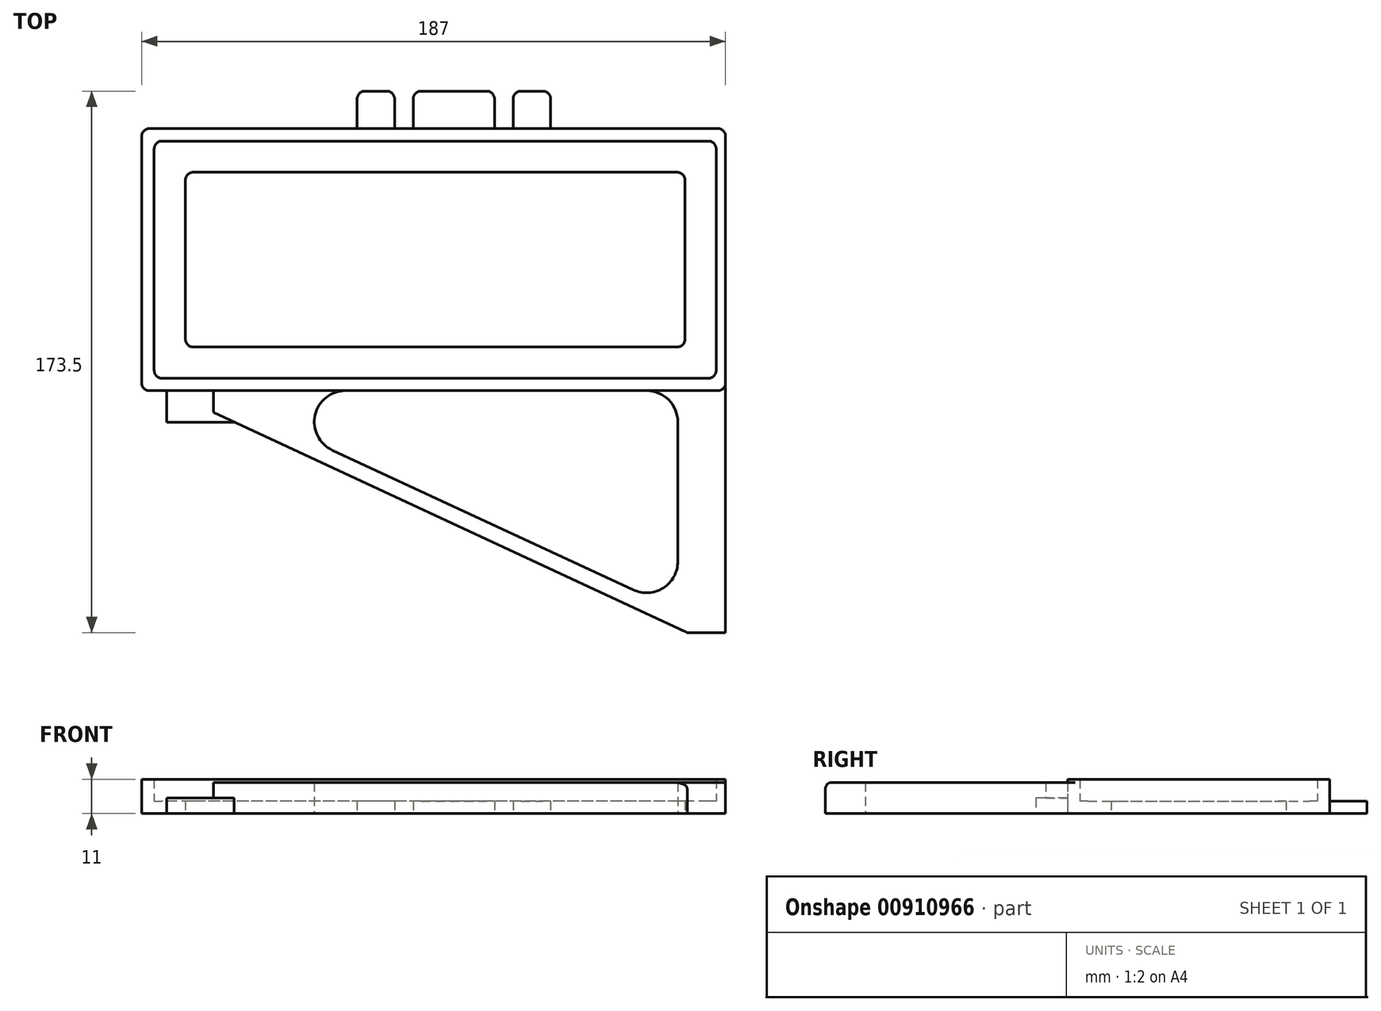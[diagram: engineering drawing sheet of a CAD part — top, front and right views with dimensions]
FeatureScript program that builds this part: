
annotation { "Feature Type Name" : "Feature", "Feature Type Description" : "" }
export const myFeature = defineFeature(function(context is Context, id is Id, definition is map)
    precondition{}
    {
        {
            var Q0;
            Q0=qCreatedBy(makeId("Top.planeOp"),FACE);
            var sketch = newSketch(context, id + "F0", { "sketchPlane" : qUnion([Q0])});
            skLineSegment(sketch, "E0.bottom", {"start": v(87.5, 0) * mm, "end": v(-87.5, 0) * mm});
            skLineSegment(sketch, "E0.top", {"start": v(87.5, 76) * mm, "end": v(-87.5, 76) * mm});
            skLineSegment(sketch, "E0.left", {"start": v(90, 2.5) * mm, "end": v(90, 73.5) * mm});
            skLineSegment(sketch, "E0.right", {"start": v(-90, 2.5) * mm, "end": v(-90, 73.5) * mm});
            skLineSegment(sketch, "E1.0", {"start": v(102, 80) * mm, "end": v(-74, 80) * mm});
            skLineSegment(sketch, "E2.0", {"start": v(-94, 0) * mm, "end": v(-94, 76) * mm});
            skLineSegment(sketch, "E3.0", {"start": v(67.7, -4) * mm, "end": v(-28.7, -4) * mm});
            skLineSegment(sketch, "E4.0", {"start": v(93, 0) * mm, "end": v(93, 76) * mm});
            skLineSegment(sketch, "E5", {"start": v(-74, 80) * mm, "end": v(-91.5, 80) * mm});
            skLineSegment(sketch, "E6", {"start": v(-94, 76) * mm, "end": v(-94, 77.5) * mm});
            skLineSegment(sketch, "E7", {"start": v(-94, -1.5) * mm, "end": v(-94, 0) * mm});
            skLineSegment(sketch, "E8", {"start": v(-88, -4) * mm, "end": v(-91.5, -4) * mm});
            skLineSegment(sketch, "E9", {"start": v(90.5, 80) * mm, "end": v(102, 80) * mm});
            skLineSegment(sketch, "E10", {"start": v(93, 77.5) * mm, "end": v(93, 76) * mm});
            skLineSegment(sketch, "E11", {"start": v(88, -4) * mm, "end": v(90.5, -4) * mm});
            skLineSegment(sketch, "E12", {"start": v(93, -1.5) * mm, "end": v(93, 0) * mm});
            skLineSegment(sketch, "E13", {"start": v(-7, 80) * mm, "end": v(-7, 89.5) * mm});
            skLineSegment(sketch, "E14", {"start": v(-4.5, 92) * mm, "end": v(16.5, 92) * mm});
            skLineSegment(sketch, "E15", {"start": v(19, 89.5) * mm, "end": v(19, 80) * mm});
            skLineSegment(sketch, "E16", {"start": v(6, 92) * mm, "end": v(6, 80) * mm, "construction": true});
            skLineSegment(sketch, "E17", {"start": v(6, 80) * mm, "end": v(6, 76) * mm, "construction": true});
            skLineSegment(sketch, "E18", {"start": v(-13, 80) * mm, "end": v(-13, 89.5) * mm});
            skLineSegment(sketch, "E19", {"start": v(-15.5, 92) * mm, "end": v(-22.5, 92) * mm});
            skLineSegment(sketch, "E20", {"start": v(-25, 89.5) * mm, "end": v(-25, 80) * mm});
            skLineSegment(sketch, "E21", {"start": v(25, 80) * mm, "end": v(25, 89.5) * mm});
            skLineSegment(sketch, "E22", {"start": v(27.5, 92) * mm, "end": v(34.5, 92) * mm});
            skLineSegment(sketch, "E23", {"start": v(37, 89.5) * mm, "end": v(37, 80) * mm});
            skPoint(sketch, "E24.visualSharp", {"position": v(19, 92) * mm});
            skArc(sketch, "E24.filletArc", {"start": v(19, 89.5) * mm, "mid": v(18.27, 91.27) * mm, "end": v(16.5, 92) * mm});
            skPoint(sketch, "E25.visualSharp", {"position": v(-7, 92) * mm});
            skArc(sketch, "E25.filletArc", {"start": v(-4.5, 92) * mm, "mid": v(-6.27, 91.27) * mm, "end": v(-7, 89.5) * mm});
            skPoint(sketch, "E26.visualSharp", {"position": v(-13, 92) * mm});
            skArc(sketch, "E26.filletArc", {"start": v(-13, 89.5) * mm, "mid": v(-13.73, 91.27) * mm, "end": v(-15.5, 92) * mm});
            skPoint(sketch, "E27.visualSharp", {"position": v(25, 92) * mm});
            skArc(sketch, "E27.filletArc", {"start": v(27.5, 92) * mm, "mid": v(25.73, 91.27) * mm, "end": v(25, 89.5) * mm});
            skPoint(sketch, "E28.visualSharp", {"position": v(-25, 92) * mm});
            skArc(sketch, "E28.filletArc", {"start": v(-22.5, 92) * mm, "mid": v(-24.27, 91.27) * mm, "end": v(-25, 89.5) * mm});
            skPoint(sketch, "E29.visualSharp", {"position": v(37, 92) * mm});
            skArc(sketch, "E29.filletArc", {"start": v(37, 89.5) * mm, "mid": v(36.27, 91.27) * mm, "end": v(34.5, 92) * mm});
            skPoint(sketch, "E30.visualSharp", {"position": v(-90, 76) * mm});
            skArc(sketch, "E30.filletArc", {"start": v(-87.5, 76) * mm, "mid": v(-89.27, 75.27) * mm, "end": v(-90, 73.5) * mm});
            skPoint(sketch, "E31.visualSharp", {"position": v(-94, 80) * mm});
            skArc(sketch, "E31.filletArc", {"start": v(-91.5, 80) * mm, "mid": v(-93.27, 79.27) * mm, "end": v(-94, 77.5) * mm});
            skPoint(sketch, "E32.visualSharp", {"position": v(-90, 0) * mm});
            skArc(sketch, "E32.filletArc", {"start": v(-90, 2.5) * mm, "mid": v(-89.27, 0.73) * mm, "end": v(-87.5, 0) * mm});
            skPoint(sketch, "E33.visualSharp", {"position": v(-94, -4) * mm});
            skArc(sketch, "E33.filletArc", {"start": v(-94, -1.5) * mm, "mid": v(-93.27, -3.27) * mm, "end": v(-91.5, -4) * mm});
            skPoint(sketch, "E34.visualSharp", {"position": v(93, -4) * mm});
            skArc(sketch, "E34.filletArc", {"start": v(90.5, -4) * mm, "mid": v(92.27, -3.27) * mm, "end": v(93, -1.5) * mm});
            skPoint(sketch, "E35.visualSharp", {"position": v(90, 0) * mm});
            skArc(sketch, "E35.filletArc", {"start": v(87.5, 0) * mm, "mid": v(89.27, 0.73) * mm, "end": v(90, 2.5) * mm});
            skPoint(sketch, "E36.visualSharp", {"position": v(90, 76) * mm});
            skArc(sketch, "E36.filletArc", {"start": v(90, 73.5) * mm, "mid": v(89.27, 75.27) * mm, "end": v(87.5, 76) * mm});
            skPoint(sketch, "E37.visualSharp", {"position": v(93, 80) * mm});
            skArc(sketch, "E37.filletArc", {"start": v(93, 77.5) * mm, "mid": v(92.27, 79.27) * mm, "end": v(90.5, 80) * mm});
            skLineSegment(sketch, "E38.0", {"start": v(77.5, 66) * mm, "end": v(-77.5, 66) * mm});
            skLineSegment(sketch, "E39.0", {"start": v(80, 12.5) * mm, "end": v(80, 63.5) * mm});
            skLineSegment(sketch, "E40.0", {"start": v(77.5, 10) * mm, "end": v(-77.5, 10) * mm});
            skLineSegment(sketch, "E41.0", {"start": v(-80, 12.5) * mm, "end": v(-80, 63.5) * mm});
            skPoint(sketch, "E42.visualSharp", {"position": v(-80, 66) * mm});
            skArc(sketch, "E42.filletArc", {"start": v(-77.5, 66) * mm, "mid": v(-79.27, 65.27) * mm, "end": v(-80, 63.5) * mm});
            skPoint(sketch, "E43.visualSharp", {"position": v(-80, 10) * mm});
            skArc(sketch, "E43.filletArc", {"start": v(-80, 12.5) * mm, "mid": v(-79.27, 10.73) * mm, "end": v(-77.5, 10) * mm});
            skPoint(sketch, "E44.visualSharp", {"position": v(80, 66) * mm});
            skArc(sketch, "E44.filletArc", {"start": v(80, 63.5) * mm, "mid": v(79.27, 65.27) * mm, "end": v(77.5, 66) * mm});
            skPoint(sketch, "E45.visualSharp", {"position": v(80, 10) * mm});
            skArc(sketch, "E45.filletArc", {"start": v(77.5, 10) * mm, "mid": v(79.27, 10.73) * mm, "end": v(80, 12.5) * mm});
            skLineSegment(sketch, "E46", {"start": v(93, -1.5) * mm, "end": v(93, -81.5) * mm});
            skLineSegment(sketch, "E47", {"start": v(93, -81.5) * mm, "end": v(80.7, -81.5) * mm});
            skLineSegment(sketch, "E48", {"start": v(-86, -4) * mm, "end": v(-86, -14.06) * mm});
            skLineSegment(sketch, "E49", {"start": v(-86, -14.06) * mm, "end": v(-71, -14.06) * mm});
            skLineSegment(sketch, "E50", {"start": v(-71, -14.06) * mm, "end": v(-71, -4) * mm});
            skLineSegment(sketch, "E51", {"start": v(-86, -4) * mm, "end": v(80.7, -81.5) * mm});
            skLineSegment(sketch, "E52", {"start": v(63.5, -67.8) * mm, "end": v(-32.9, -23.07) * mm});
            skLineSegment(sketch, "E53", {"start": v(-71, -14.06) * mm, "end": v(-64.36, -14.06) * mm});
            skArc(sketch, "E54.filletArc", {"start": v(77.7, -14) * mm, "mid": v(74.78, -6.93) * mm, "end": v(67.7, -4) * mm});
            skLineSegment(sketch, "E55", {"start": v(67.7, -4) * mm, "end": v(88, -4) * mm});
            skLineSegment(sketch, "E56", {"start": v(77.7, -14) * mm, "end": v(77.7, -58.74) * mm});
            skLineSegment(sketch, "E57", {"start": v(80.7, -74.4) * mm, "end": v(80.7, -81.5) * mm});
            skArc(sketch, "E58.filletArc", {"start": v(63.5, -67.8) * mm, "mid": v(73.09, -67.17) * mm, "end": v(77.7, -58.74) * mm});
            skPoint(sketch, "E59.newPointA", {"position": v(-88, -4) * mm});
            skArc(sketch, "E59.filletArc", {"start": v(-28.7, -4) * mm, "mid": v(-38.46, -11.84) * mm, "end": v(-32.9, -23.07) * mm});
            skLineSegment(sketch, "E60", {"start": v(-28.7, -4) * mm, "end": v(-88, -4) * mm});
            skSolve(sketch);
        }
        {
            var Q0;
            Q0=makeQuery(id+"F0.imprint","IMPRINT",FACE,{"disambiguationData":[TD([[makeQuery(id+"F0.imprint","IMPRINT",EDGE,{"derivedFrom":sQuery(id+"F0.wireOp",EDGE,"E0.bottom")}),1.0]])]});
            extrude(context, id + "F1", {"entities" : qUnion([Q0]), "depth" : 11 * mm, "offsetDistance" : 25 * mm});
        }
        {
            var Q0;
            Q0=makeQuery(id+"F0.imprint","IMPRINT",FACE,{"disambiguationData":[TD([[makeQuery(id+"F0.imprint","IMPRINT",EDGE,{"derivedFrom":sQuery(id+"F0.wireOp",EDGE,"E0.bottom")}),-1.0]])]});
            var Q1;
            {var subQ1=sQuery(id+"F0.wireOp",EDGE,"E18");Q1=makeQuery(id+"F0.imprint","IMPRINT",FACE,{"disambiguationData":[TD([[makeQuery(id+"F0.imprint","IMPRINT",EDGE,{"derivedFrom":subQ1}),1.0]])]});}
            var Q2;
            {var subQ1=sQuery(id+"F0.wireOp",EDGE,"E13");Q2=makeQuery(id+"F0.imprint","IMPRINT",FACE,{"disambiguationData":[TD([[makeQuery(id+"F0.imprint","IMPRINT",EDGE,{"derivedFrom":subQ1}),-1.0]])]});}
            var Q3;
            {var subQ0=sQuery(id+"F0.wireOp",EDGE,"E21");Q3=makeQuery(id+"F0.imprint","IMPRINT",FACE,{"disambiguationData":[TD([[makeQuery(id+"F0.imprint","IMPRINT",EDGE,{"derivedFrom":subQ0}),-1.0]])]});}
            extrude(context, id + "F2", {"entities" : qUnion([Q0, Q1, Q2, Q3]), "operationType" : NewBodyOperationType.ADD, "depth" : 4 * mm, "offsetDistance" : 25 * mm});
        }
        {
            var Q0;
            {var subQ0=sQuery(id+"F0.wireOp",EDGE,"E11");Q0=makeQuery(id+"F0.imprint","IMPRINT",FACE,{"disambiguationData":[TD([[makeQuery(id+"F0.imprint","IMPRINT",EDGE,{"derivedFrom":subQ0}),-1.0]])]});}
            var Q1;
            {var subQ0=sQuery(id+"F0.wireOp",EDGE,"E47");Q1=makeQuery(id+"F0.imprint","IMPRINT",FACE,{"disambiguationData":[TD([[makeQuery(id+"F0.imprint","IMPRINT",EDGE,{"derivedFrom":subQ0}),-1.0]])]});}
            extrude(context, id + "F3", {"entities" : qUnion([Q0, Q1]), "operationType" : NewBodyOperationType.ADD, "depth" : 10 * mm, "offsetDistance" : 25 * mm});
        }
        {
            var Q0;
            {var subQ0=sQuery(id+"F0.wireOp",EDGE,"E48");Q0=makeQuery(id+"F0.imprint","IMPRINT",FACE,{"disambiguationData":[TD([[makeQuery(id+"F0.imprint","IMPRINT",EDGE,{"derivedFrom":subQ0}),1.0]])]});}
            var Q1;
            {var subQ1=sQuery(id+"F0.wireOp",EDGE,"Ny0Gnn2i-Ygqb-VPq2-N1I1-QU3OLZ8xniGR");var subQ3=sQuery(id+"F0.wireOp",EDGE,"E52");var subQ4=makeQuery(id+"F0.imprint","INTERSECT",VERTEX,{"derivedFrom":[subQ1,subQ3]});Q1=makeQuery(id+"F0.imprint","IMPRINT",FACE,{"disambiguationData":[TD([[makeQuery(id+"F0.imprint","IMPRINT",EDGE,{"disambiguationData":[TD([[subQ4,1.0]])],"derivedFrom":subQ1}),1.0]])]});}
            var Q2;
            {var subQ0=sQuery(id+"F0.wireOp",EDGE,"E60");var subQ5=sQuery(id+"F0.wireOp",EDGE,"E50");var subQ6=makeQuery(id+"F0.imprint","INTERSECT",VERTEX,{"derivedFrom":[subQ5,subQ0]});Q2=makeQuery(id+"F0.imprint","IMPRINT",FACE,{"disambiguationData":[TD([[makeQuery(id+"F0.imprint","IMPRINT",EDGE,{"disambiguationData":[TD([[subQ6,1.0]])],"derivedFrom":subQ5}),1.0]])]});}
            var Q3;
            {var subQ0=sQuery(id+"F0.wireOp",EDGE,"E53");Q3=makeQuery(id+"F0.imprint","IMPRINT",FACE,{"disambiguationData":[TD([[makeQuery(id+"F0.imprint","IMPRINT",EDGE,{"derivedFrom":subQ0}),1.0]])]});}
            extrude(context, id + "F4", {"entities" : qUnion([Q0, Q1, Q2, Q3]), "operationType" : NewBodyOperationType.ADD, "depth" : 5 * mm, "offsetDistance" : 25 * mm});
        }
        {
            var Q0;
            Q0=makeQuery(id+"F3.opExtrude","CAP_EDGE",EDGE,{"disambiguationData":[OSD([sQuery(id+"F0.wireOp",EDGE,"E47")])],"isStart":false});
            fillet(context, id + "F5", {"entities" : qUnion([Q0]), "radius" : 2 * mm, "tangentPropagation" : true, "allowEdgeOverflow" : false});
        }
    });
